# Revit family: Haworth_Tibas_Desk_LShape_AP_PRELIMINARY1
name_source: partatom
category: Furniture
units: mm (PartAtom-declared; Revit-internal decimal feet)

## family parameters
Always vertical = Yes
Cut with Voids When Loaded = No
OmniClass Number = 23.40.70.14.64.11
OmniClass Title = Office Furniture
Room Calculation Point = No
Shared = No
Work Plane-Based = No

## types (7) — shared parameters
Actual Height = 835 mm
Assembly Code = E2020200
Back Leg Offset = 150 mm
Cable Tray Finish = Haworth _ Paint _ Metallic Silver
Description = Haworth - Tibas - Desk - L-Shape
Leg Height = 800 mm  [stored 2.62467 ft]
Manufacturer = Haworth
Model = SYTBLSXXXX
Product URL = https://www.haworth.com
Revision Number = 1
Size = Verify Final Dim.w/ Haworth
Trim Finish = Haworth _ Polymer _ Undecided
URL = https://www.haworth.com
Warranty = http://www.haworth.com
With Top = Yes
Worksurface Depth = 600, 700, 750mm
Worksurface Width = 1200, 1400, 1500, 1600

## per-type parameters (varying)
| type | Accessory Kit | Actual Depth | Actual Length | Actual Width | Beam Width R | Cable Tray Single | Cable Tray Width | Depth | Flip Top Cable Outlet | Flip Top Width | No Accessory Kit | Round Cable Outlet |
| 1500/600 x 1500/600 | Yes | 600 mm | 1500 mm  [stored 4.92126 ft] | 1500 mm  [stored 4.92126 ft] | 1350 mm | Yes | 1200 mm | 600 mm | Yes | 200 mm  [stored 0.656168 ft] | No | No |
| 1600/600 x 1200/600 | Yes | 600 mm | 1200 mm | 1600 mm  [stored 5.24934 ft] | 1450 mm | Yes | 900 mm  [stored 2.95276 ft] | 600 mm | No | 200 mm  [stored 0.656168 ft] | No | Yes |
| 1600/600 x 1400/600 | No | 600 mm | 1400 mm | 1600 mm  [stored 5.24934 ft] | 1450 mm | No | 1100 mm  [stored 3.60892 ft] | 600 mm | No | 200 mm  [stored 0.656168 ft] | Yes | No |
| 1600/600 x 1600/600 | Yes | 600 mm | 1600 mm  [stored 5.24934 ft] | 1600 mm  [stored 5.24934 ft] | 1450 mm | Yes | 1300 mm  [stored 4.26509 ft] | 600 mm | Yes | 200 mm  [stored 0.656168 ft] | No | No |
| 1600/700 x 1600/700 | Yes | 700 mm | 1600 mm  [stored 5.24934 ft] | 1600 mm  [stored 5.24934 ft] | 1450 mm | Yes | 1300 mm  [stored 4.26509 ft] | 700 mm | No | 200 mm  [stored 0.656168 ft] | No | Yes |
| 1600/750 x 1600/600 | No | 600 mm | 1600 mm  [stored 5.24934 ft] | 1600 mm  [stored 5.24934 ft] | 1450 mm | No | 1300 mm  [stored 4.26509 ft] | 750 mm  [stored 2.46063 ft] | No | 400 mm  [stored 1.31234 ft] | Yes | No |
| 1600/750 x 1600/750 | Yes | 750 mm  [stored 2.46063 ft] | 1600 mm  [stored 5.24934 ft] | 1600 mm  [stored 5.24934 ft] | 1450 mm | Yes | 1300 mm  [stored 4.26509 ft] | 750 mm  [stored 2.46063 ft] | Yes | 400 mm  [stored 1.31234 ft] | No | No |

type visibility flags: 7 boolean params named "<type name>" — each type sets only its own to Yes (folded from table)

note: [stored X ft] marks values corroborated as IEEE doubles in the binary element streams (Revit-internal decimal feet)

## geometry (parser evidence)
native form markers: Sweep x15
no freeform markers — native parametric forms only
